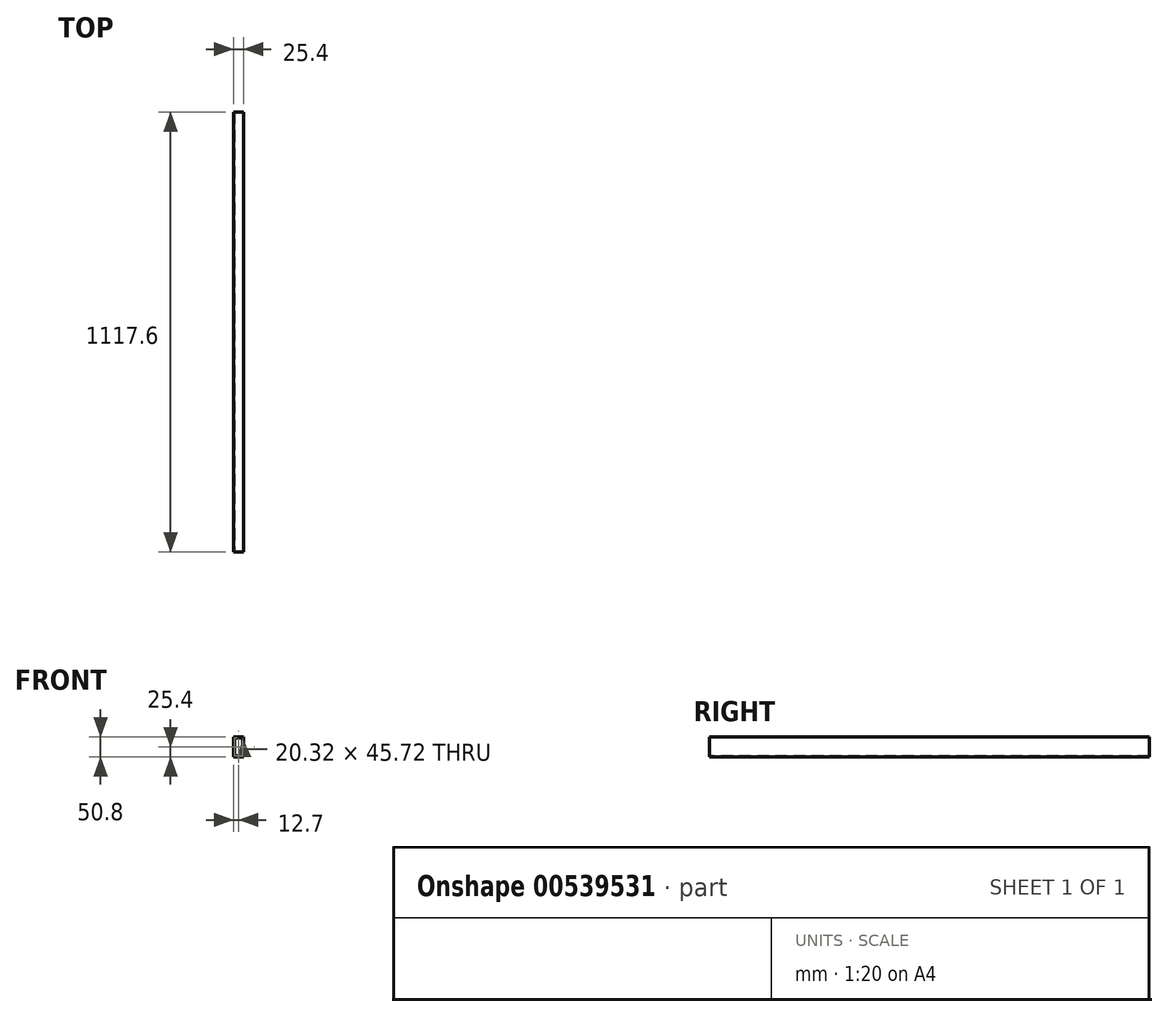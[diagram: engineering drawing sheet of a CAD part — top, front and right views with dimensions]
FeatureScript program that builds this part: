
annotation { "Feature Type Name" : "Feature", "Feature Type Description" : "" }
export const myFeature = defineFeature(function(context is Context, id is Id, definition is map)
    precondition{}
    {
        {
            var Q0;
            Q0=qCreatedBy(makeId("Front.planeOp"),FACE);
            var sketch = newSketch(context, id + "F0", { "sketchPlane" : qUnion([Q0])});
            skLineSegment(sketch, "E0.bottom", {"start": v(12.7, -25.4) * mm, "end": v(-12.7, -25.4) * mm});
            skLineSegment(sketch, "E0.top", {"start": v(12.7, 25.4) * mm, "end": v(-12.7, 25.4) * mm});
            skLineSegment(sketch, "E0.left", {"start": v(12.7, -25.4) * mm, "end": v(12.7, 25.4) * mm});
            skLineSegment(sketch, "E0.right", {"start": v(-12.7, -25.4) * mm, "end": v(-12.7, 25.4) * mm});
            skPoint(sketch, "E0.middle", {"position": v(0, 0) * mm});
            skSolve(sketch);
        }
        {
            var Q0;
            Q0=makeQuery(id+"F0.imprint","IMPRINT",FACE,{"disambiguationData":[TD([[makeQuery(id+"F0.imprint","IMPRINT",EDGE,{"derivedFrom":sQuery(id+"F0.wireOp",EDGE,"E0.bottom")}),-1.0]])]});
            extrude(context, id + "F1", {"entities" : qUnion([Q0]), "depth" : 1117.6 * mm, "offsetDistance" : 25.4 * mm});
        }
        {
            var Q0;
            Q0=makeQuery(id+"F1.opExtrude","CAP_FACE",FACE,{"disambiguationData":[OSD([sQuery(id+"F0.wireOp",EDGE,"E0.bottom"),sQuery(id+"F0.wireOp",EDGE,"E0.top"),sQuery(id+"F0.wireOp",EDGE,"E0.left"),sQuery(id+"F0.wireOp",EDGE,"E0.right")])],"isStart":false});
            var sketch = newSketch(context, id + "F2", { "sketchPlane" : qUnion([Q0])});
            skLineSegment(sketch, "E1.bottom", {"start": v(10.16, -22.86) * mm, "end": v(-10.16, -22.86) * mm});
            skLineSegment(sketch, "E1.top", {"start": v(10.16, 22.86) * mm, "end": v(-10.16, 22.86) * mm});
            skLineSegment(sketch, "E1.left", {"start": v(10.16, -22.86) * mm, "end": v(10.16, 22.86) * mm});
            skLineSegment(sketch, "E1.right", {"start": v(-10.16, -22.86) * mm, "end": v(-10.16, 22.86) * mm});
            skPoint(sketch, "E1.middle", {"position": v(0, 0) * mm});
            skSolve(sketch);
        }
        {
            var Q0;
            Q0=makeQuery(id+"F2.imprint","IMPRINT",FACE,{"disambiguationData":[TD([[makeQuery(id+"F2.imprint","IMPRINT",EDGE,{"derivedFrom":sQuery(id+"F2.wireOp",EDGE,"E1.bottom")}),-1.0]])]});
            extrude(context, id + "F3", {"entities" : qUnion([Q0]), "operationType" : NewBodyOperationType.REMOVE, "endBound" : BoundingType.THROUGH_ALL, "oppositeDirection" : true, "depth" : 25.4 * mm});
        }
    });
